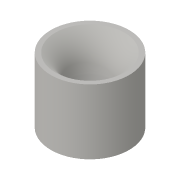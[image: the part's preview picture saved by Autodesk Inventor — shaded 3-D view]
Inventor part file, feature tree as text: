
AUTODESK INVENTOR PART (.ipt)
format: ipt  version: 2016 SP1 (Build 200210100, 210)  size: 146,432 bytes
history: native  units: in
note: dims shown in document units (in); Inventor stores cm internally (conversion verified against a paired STEP export)
features: revolve x1, sketch x1
ambient origin geometry x8: Origin, YZ Plane, XZ Plane, XY Plane, X Axis, Y Axis, Z Axis, Center Point
bodies: Solid1 (feature_tree)
feature tree (2):
  revolve  "Revolution1"  [1 undecoded]
  sketch  "Sketch1"  dims[d5=0.5in d7=0.25in d8=105.0deg d23=2.9994in d26=1.25in d30=90.0deg d33=0.25in d51=0.25in d54=0.25in d55=0.625in d56=0.2731in d57=0.625in d60=0.1718in d62=1.13in d63=2.15in d64=0.2483in d65=90.0deg]
note: 1 required parameter value undecoded (feature->parameter linkage not recoverable at this tier; creation-order binding heuristic only, values carry confidence <= 0.55)
